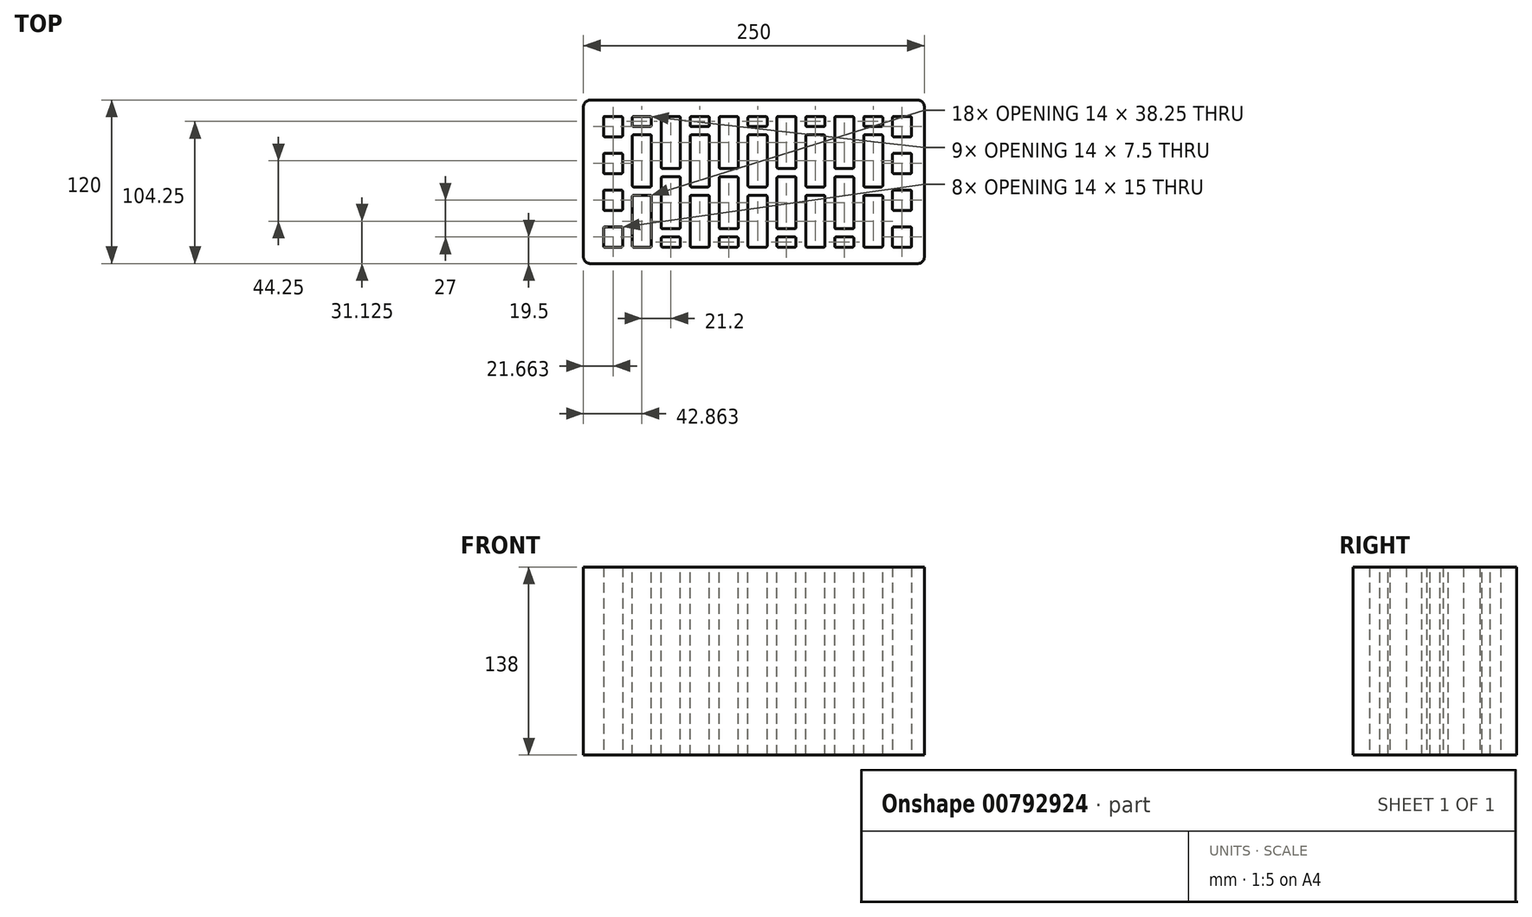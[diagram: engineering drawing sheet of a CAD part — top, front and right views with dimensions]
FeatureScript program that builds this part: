
annotation { "Feature Type Name" : "Feature", "Feature Type Description" : "" }
export const myFeature = defineFeature(function(context is Context, id is Id, definition is map)
    precondition{}
    {
        {
            var Q0;
            Q0=qCreatedBy(makeId("Top.planeOp"),FACE);
            var sketch = newSketch(context, id + "F0", { "sketchPlane" : qUnion([Q0])});
            skLineSegment(sketch, "E0.bottom", {"start": v(120, 60) * mm, "end": v(-120, 60) * mm});
            skLineSegment(sketch, "E0.top", {"start": v(120, -60) * mm, "end": v(-120, -60) * mm});
            skLineSegment(sketch, "E0.left", {"start": v(125, 55) * mm, "end": v(125, -55) * mm});
            skLineSegment(sketch, "E0.right", {"start": v(-125, 55) * mm, "end": v(-125, -55) * mm});
            skPoint(sketch, "E0.middle", {"position": v(0, 0) * mm});
            skPoint(sketch, "E1.visualSharp", {"position": v(-125, 60) * mm});
            skArc(sketch, "E1.filletArc", {"start": v(-120, 60) * mm, "mid": v(-123.54, 58.54) * mm, "end": v(-125, 55) * mm});
            skPoint(sketch, "E2.visualSharp", {"position": v(-125, -60) * mm});
            skArc(sketch, "E2.filletArc", {"start": v(-125, -55) * mm, "mid": v(-123.54, -58.54) * mm, "end": v(-120, -60) * mm});
            skPoint(sketch, "E3.visualSharp", {"position": v(125, -60) * mm});
            skArc(sketch, "E3.filletArc", {"start": v(120, -60) * mm, "mid": v(123.54, -58.54) * mm, "end": v(125, -55) * mm});
            skPoint(sketch, "E4.visualSharp", {"position": v(125, 60) * mm});
            skArc(sketch, "E4.filletArc", {"start": v(125, 55) * mm, "mid": v(123.54, 58.54) * mm, "end": v(120, 60) * mm});
            skLineSegment(sketch, "E5.bottom", {"start": v(-97.34, 48) * mm, "end": v(-109.34, 48) * mm});
            skLineSegment(sketch, "E5.top", {"start": v(-97.34, 33) * mm, "end": v(-109.34, 33) * mm});
            skLineSegment(sketch, "E5.left", {"start": v(-96.34, 47) * mm, "end": v(-96.34, 34) * mm});
            skLineSegment(sketch, "E5.right", {"start": v(-110.34, 47) * mm, "end": v(-110.34, 34) * mm});
            skPoint(sketch, "E5.middle", {"position": v(-103.34, 40.5) * mm});
            skPoint(sketch, "E6.visualSharp", {"position": v(-110.34, 48) * mm});
            skArc(sketch, "E6.filletArc", {"start": v(-109.34, 48) * mm, "mid": v(-110.04, 47.7) * mm, "end": v(-110.34, 47) * mm});
            skPoint(sketch, "E7.visualSharp", {"position": v(-96.34, 48) * mm});
            skArc(sketch, "E7.filletArc", {"start": v(-96.34, 47) * mm, "mid": v(-96.63, 47.7) * mm, "end": v(-97.34, 48) * mm});
            skPoint(sketch, "E8.visualSharp", {"position": v(-96.34, 33) * mm});
            skArc(sketch, "E8.filletArc", {"start": v(-97.34, 33) * mm, "mid": v(-96.63, 33.3) * mm, "end": v(-96.34, 34) * mm});
            skPoint(sketch, "E9.visualSharp", {"position": v(-110.34, 33) * mm});
            skArc(sketch, "E9.filletArc", {"start": v(-110.34, 34) * mm, "mid": v(-110.04, 33.3) * mm, "end": v(-109.34, 33) * mm});
            skPoint(sketch, "E10.0.1.0", {"position": v(-103.34, 13.5) * mm});
            skLineSegment(sketch, "E10.0.1.1", {"start": v(-97.34, 21) * mm, "end": v(-109.34, 21) * mm});
            skPoint(sketch, "E10.0.1.2", {"position": v(-110.34, 6) * mm});
            skLineSegment(sketch, "E10.0.1.3", {"start": v(-97.34, 6) * mm, "end": v(-109.34, 6) * mm});
            skLineSegment(sketch, "E10.0.1.4", {"start": v(-96.34, 20) * mm, "end": v(-96.34, 7) * mm});
            skLineSegment(sketch, "E10.0.1.5", {"start": v(-110.34, 20) * mm, "end": v(-110.34, 7) * mm});
            skPoint(sketch, "E10.0.1.6", {"position": v(-110.34, 21) * mm});
            skPoint(sketch, "E10.0.1.7", {"position": v(-96.34, 21) * mm});
            skPoint(sketch, "E10.0.1.8", {"position": v(-96.34, 6) * mm});
            skArc(sketch, "E10.0.1.9", {"start": v(-97.34, 6) * mm, "mid": v(-96.63, 6.3) * mm, "end": v(-96.34, 7) * mm});
            skArc(sketch, "E10.0.1.10", {"start": v(-110.34, 7) * mm, "mid": v(-110.04, 6.3) * mm, "end": v(-109.34, 6) * mm});
            skArc(sketch, "E10.0.1.11", {"start": v(-109.34, 21) * mm, "mid": v(-110.04, 20.7) * mm, "end": v(-110.34, 20) * mm});
            skArc(sketch, "E10.0.1.12", {"start": v(-96.34, 20) * mm, "mid": v(-96.63, 20.7) * mm, "end": v(-97.34, 21) * mm});
            skPoint(sketch, "E10.0.2.0", {"position": v(-103.34, -13.5) * mm});
            skLineSegment(sketch, "E10.0.2.1", {"start": v(-97.34, -6) * mm, "end": v(-109.34, -6) * mm});
            skPoint(sketch, "E10.0.2.2", {"position": v(-110.34, -21) * mm});
            skLineSegment(sketch, "E10.0.2.3", {"start": v(-97.34, -21) * mm, "end": v(-109.34, -21) * mm});
            skLineSegment(sketch, "E10.0.2.4", {"start": v(-96.34, -7) * mm, "end": v(-96.34, -20) * mm});
            skLineSegment(sketch, "E10.0.2.5", {"start": v(-110.34, -7) * mm, "end": v(-110.34, -20) * mm});
            skPoint(sketch, "E10.0.2.6", {"position": v(-110.34, -6) * mm});
            skPoint(sketch, "E10.0.2.7", {"position": v(-96.34, -6) * mm});
            skPoint(sketch, "E10.0.2.8", {"position": v(-96.34, -21) * mm});
            skArc(sketch, "E10.0.2.9", {"start": v(-97.34, -21) * mm, "mid": v(-96.63, -20.7) * mm, "end": v(-96.34, -20) * mm});
            skArc(sketch, "E10.0.2.10", {"start": v(-110.34, -20) * mm, "mid": v(-110.04, -20.7) * mm, "end": v(-109.34, -21) * mm});
            skArc(sketch, "E10.0.2.11", {"start": v(-109.34, -6) * mm, "mid": v(-110.04, -6.3) * mm, "end": v(-110.34, -7) * mm});
            skArc(sketch, "E10.0.2.12", {"start": v(-96.34, -7) * mm, "mid": v(-96.63, -6.3) * mm, "end": v(-97.34, -6) * mm});
            skPoint(sketch, "E10.0.3.0", {"position": v(-103.34, -40.5) * mm});
            skLineSegment(sketch, "E10.0.3.1", {"start": v(-97.34, -33) * mm, "end": v(-109.34, -33) * mm});
            skPoint(sketch, "E10.0.3.2", {"position": v(-110.34, -48) * mm});
            skLineSegment(sketch, "E10.0.3.3", {"start": v(-97.34, -48) * mm, "end": v(-109.34, -48) * mm});
            skLineSegment(sketch, "E10.0.3.4", {"start": v(-96.34, -34) * mm, "end": v(-96.34, -47) * mm});
            skLineSegment(sketch, "E10.0.3.5", {"start": v(-110.34, -34) * mm, "end": v(-110.34, -47) * mm});
            skPoint(sketch, "E10.0.3.6", {"position": v(-110.34, -33) * mm});
            skPoint(sketch, "E10.0.3.7", {"position": v(-96.34, -33) * mm});
            skPoint(sketch, "E10.0.3.8", {"position": v(-96.34, -48) * mm});
            skArc(sketch, "E10.0.3.9", {"start": v(-97.34, -48) * mm, "mid": v(-96.63, -47.7) * mm, "end": v(-96.34, -47) * mm});
            skArc(sketch, "E10.0.3.10", {"start": v(-110.34, -47) * mm, "mid": v(-110.04, -47.7) * mm, "end": v(-109.34, -48) * mm});
            skArc(sketch, "E10.0.3.11", {"start": v(-109.34, -33) * mm, "mid": v(-110.04, -33.3) * mm, "end": v(-110.34, -34) * mm});
            skArc(sketch, "E10.0.3.12", {"start": v(-96.34, -34) * mm, "mid": v(-96.63, -33.3) * mm, "end": v(-97.34, -33) * mm});
            skPoint(sketch, "E10.1.0.0", {"position": v(108.66, 40.5) * mm});
            skLineSegment(sketch, "E10.1.0.1", {"start": v(114.66, 48) * mm, "end": v(102.66, 48) * mm});
            skPoint(sketch, "E10.1.0.2", {"position": v(101.66, 33) * mm});
            skLineSegment(sketch, "E10.1.0.3", {"start": v(114.66, 33) * mm, "end": v(102.66, 33) * mm});
            skLineSegment(sketch, "E10.1.0.4", {"start": v(115.66, 47) * mm, "end": v(115.66, 34) * mm});
            skLineSegment(sketch, "E10.1.0.5", {"start": v(101.66, 47) * mm, "end": v(101.66, 34) * mm});
            skPoint(sketch, "E10.1.0.6", {"position": v(101.66, 48) * mm});
            skPoint(sketch, "E10.1.0.7", {"position": v(115.66, 48) * mm});
            skPoint(sketch, "E10.1.0.8", {"position": v(115.66, 33) * mm});
            skArc(sketch, "E10.1.0.9", {"start": v(114.66, 33) * mm, "mid": v(115.37, 33.3) * mm, "end": v(115.66, 34) * mm});
            skArc(sketch, "E10.1.0.10", {"start": v(101.66, 34) * mm, "mid": v(101.96, 33.3) * mm, "end": v(102.66, 33) * mm});
            skArc(sketch, "E10.1.0.11", {"start": v(102.66, 48) * mm, "mid": v(101.96, 47.7) * mm, "end": v(101.66, 47) * mm});
            skArc(sketch, "E10.1.0.12", {"start": v(115.66, 47) * mm, "mid": v(115.37, 47.7) * mm, "end": v(114.66, 48) * mm});
            skPoint(sketch, "E10.1.1.0", {"position": v(108.66, 13.5) * mm});
            skLineSegment(sketch, "E10.1.1.1", {"start": v(114.66, 21) * mm, "end": v(102.66, 21) * mm});
            skPoint(sketch, "E10.1.1.2", {"position": v(101.66, 6) * mm});
            skLineSegment(sketch, "E10.1.1.3", {"start": v(114.66, 6) * mm, "end": v(102.66, 6) * mm});
            skLineSegment(sketch, "E10.1.1.4", {"start": v(115.66, 20) * mm, "end": v(115.66, 7) * mm});
            skLineSegment(sketch, "E10.1.1.5", {"start": v(101.66, 20) * mm, "end": v(101.66, 7) * mm});
            skPoint(sketch, "E10.1.1.6", {"position": v(101.66, 21) * mm});
            skPoint(sketch, "E10.1.1.7", {"position": v(115.66, 21) * mm});
            skPoint(sketch, "E10.1.1.8", {"position": v(115.66, 6) * mm});
            skArc(sketch, "E10.1.1.9", {"start": v(114.66, 6) * mm, "mid": v(115.37, 6.3) * mm, "end": v(115.66, 7) * mm});
            skArc(sketch, "E10.1.1.10", {"start": v(101.66, 7) * mm, "mid": v(101.96, 6.3) * mm, "end": v(102.66, 6) * mm});
            skArc(sketch, "E10.1.1.11", {"start": v(102.66, 21) * mm, "mid": v(101.96, 20.7) * mm, "end": v(101.66, 20) * mm});
            skArc(sketch, "E10.1.1.12", {"start": v(115.66, 20) * mm, "mid": v(115.37, 20.7) * mm, "end": v(114.66, 21) * mm});
            skPoint(sketch, "E10.1.2.0", {"position": v(108.66, -13.5) * mm});
            skLineSegment(sketch, "E10.1.2.1", {"start": v(114.66, -6) * mm, "end": v(102.66, -6) * mm});
            skPoint(sketch, "E10.1.2.2", {"position": v(101.66, -21) * mm});
            skLineSegment(sketch, "E10.1.2.3", {"start": v(114.66, -21) * mm, "end": v(102.66, -21) * mm});
            skLineSegment(sketch, "E10.1.2.4", {"start": v(115.66, -7) * mm, "end": v(115.66, -20) * mm});
            skLineSegment(sketch, "E10.1.2.5", {"start": v(101.66, -7) * mm, "end": v(101.66, -20) * mm});
            skPoint(sketch, "E10.1.2.6", {"position": v(101.66, -6) * mm});
            skPoint(sketch, "E10.1.2.7", {"position": v(115.66, -6) * mm});
            skPoint(sketch, "E10.1.2.8", {"position": v(115.66, -21) * mm});
            skArc(sketch, "E10.1.2.9", {"start": v(114.66, -21) * mm, "mid": v(115.37, -20.7) * mm, "end": v(115.66, -20) * mm});
            skArc(sketch, "E10.1.2.10", {"start": v(101.66, -20) * mm, "mid": v(101.96, -20.7) * mm, "end": v(102.66, -21) * mm});
            skArc(sketch, "E10.1.2.11", {"start": v(102.66, -6) * mm, "mid": v(101.96, -6.3) * mm, "end": v(101.66, -7) * mm});
            skArc(sketch, "E10.1.2.12", {"start": v(115.66, -7) * mm, "mid": v(115.37, -6.3) * mm, "end": v(114.66, -6) * mm});
            skPoint(sketch, "E10.1.3.0", {"position": v(108.66, -40.5) * mm});
            skLineSegment(sketch, "E10.1.3.1", {"start": v(114.66, -33) * mm, "end": v(102.66, -33) * mm});
            skPoint(sketch, "E10.1.3.2", {"position": v(101.66, -48) * mm});
            skLineSegment(sketch, "E10.1.3.3", {"start": v(114.66, -48) * mm, "end": v(102.66, -48) * mm});
            skLineSegment(sketch, "E10.1.3.4", {"start": v(115.66, -34) * mm, "end": v(115.66, -47) * mm});
            skLineSegment(sketch, "E10.1.3.5", {"start": v(101.66, -34) * mm, "end": v(101.66, -47) * mm});
            skPoint(sketch, "E10.1.3.6", {"position": v(101.66, -33) * mm});
            skPoint(sketch, "E10.1.3.7", {"position": v(115.66, -33) * mm});
            skPoint(sketch, "E10.1.3.8", {"position": v(115.66, -48) * mm});
            skArc(sketch, "E10.1.3.9", {"start": v(114.66, -48) * mm, "mid": v(115.37, -47.7) * mm, "end": v(115.66, -47) * mm});
            skArc(sketch, "E10.1.3.10", {"start": v(101.66, -47) * mm, "mid": v(101.96, -47.7) * mm, "end": v(102.66, -48) * mm});
            skArc(sketch, "E10.1.3.11", {"start": v(102.66, -33) * mm, "mid": v(101.96, -33.3) * mm, "end": v(101.66, -34) * mm});
            skArc(sketch, "E10.1.3.12", {"start": v(115.66, -34) * mm, "mid": v(115.37, -33.3) * mm, "end": v(114.66, -33) * mm});
            skLineSegment(sketch, "E10.direction1", {"start": v(-110.34, 33) * mm, "end": v(101.66, 33) * mm, "construction": true});
            skLineSegment(sketch, "E10.direction2", {"start": v(-110.34, 33) * mm, "end": v(-110.34, 6) * mm, "construction": true});
            skLineSegment(sketch, "E11", {"start": v(-103.56, -60) * mm, "end": v(-103.56, -48) * mm, "construction": true});
            skLineSegment(sketch, "E12", {"start": v(-103.34, -33) * mm, "end": v(-103.34, -21) * mm, "construction": true});
            skLineSegment(sketch, "E13", {"start": v(-103.34, -6) * mm, "end": v(-103.34, 6) * mm, "construction": true});
            skLineSegment(sketch, "E14", {"start": v(-103.34, 21) * mm, "end": v(-103.34, 33) * mm, "construction": true});
            skLineSegment(sketch, "E15", {"start": v(-103.34, 48) * mm, "end": v(-103.34, 60) * mm, "construction": true});
            skSolve(sketch);
        }
        {
            var Q0;
            Q0=makeQuery(id+"F0.imprint","IMPRINT",FACE,{"disambiguationData":[TD([[makeQuery(id+"F0.imprint","IMPRINT",EDGE,{"derivedFrom":sQuery(id+"F0.wireOp",EDGE,"E0.bottom")}),1.0]])]});
            extrude(context, id + "F1", {"entities" : qUnion([Q0]), "depth" : 138 * mm, "offsetDistance" : 25 * mm});
        }
        {
            var Q0;
            Q0=makeQuery(id+"F1.opExtrude","CAP_FACE",FACE,{"disambiguationData":[OSD([sQuery(id+"F0.wireOp",EDGE,"E0.bottom"),sQuery(id+"F0.wireOp",EDGE,"E0.top"),sQuery(id+"F0.wireOp",EDGE,"E0.left"),sQuery(id+"F0.wireOp",EDGE,"E0.right"),sQuery(id+"F0.wireOp",EDGE,"E1.filletArc"),sQuery(id+"F0.wireOp",EDGE,"E2.filletArc"),sQuery(id+"F0.wireOp",EDGE,"E3.filletArc"),sQuery(id+"F0.wireOp",EDGE,"E4.filletArc"),sQuery(id+"F0.wireOp",EDGE,"E5.bottom"),sQuery(id+"F0.wireOp",EDGE,"E5.top"),sQuery(id+"F0.wireOp",EDGE,"E5.left"),sQuery(id+"F0.wireOp",EDGE,"E5.right"),sQuery(id+"F0.wireOp",EDGE,"E6.filletArc"),sQuery(id+"F0.wireOp",EDGE,"E7.filletArc"),sQuery(id+"F0.wireOp",EDGE,"E8.filletArc"),sQuery(id+"F0.wireOp",EDGE,"E9.filletArc"),sQuery(id+"F0.wireOp",EDGE,"E10.0.1.1"),sQuery(id+"F0.wireOp",EDGE,"E10.0.1.3"),sQuery(id+"F0.wireOp",EDGE,"E10.0.1.4"),sQuery(id+"F0.wireOp",EDGE,"E10.0.1.5"),sQuery(id+"F0.wireOp",EDGE,"E10.0.1.9"),sQuery(id+"F0.wireOp",EDGE,"E10.0.1.10"),sQuery(id+"F0.wireOp",EDGE,"E10.0.1.11"),sQuery(id+"F0.wireOp",EDGE,"E10.0.1.12"),sQuery(id+"F0.wireOp",EDGE,"E10.0.2.1"),sQuery(id+"F0.wireOp",EDGE,"E10.0.2.3"),sQuery(id+"F0.wireOp",EDGE,"E10.0.2.4"),sQuery(id+"F0.wireOp",EDGE,"E10.0.2.5"),sQuery(id+"F0.wireOp",EDGE,"E10.0.2.9"),sQuery(id+"F0.wireOp",EDGE,"E10.0.2.10"),sQuery(id+"F0.wireOp",EDGE,"E10.0.2.11"),sQuery(id+"F0.wireOp",EDGE,"E10.0.2.12"),sQuery(id+"F0.wireOp",EDGE,"E10.0.3.1"),sQuery(id+"F0.wireOp",EDGE,"E10.0.3.3"),sQuery(id+"F0.wireOp",EDGE,"E10.0.3.4"),sQuery(id+"F0.wireOp",EDGE,"E10.0.3.5"),sQuery(id+"F0.wireOp",EDGE,"E10.0.3.9"),sQuery(id+"F0.wireOp",EDGE,"E10.0.3.10"),sQuery(id+"F0.wireOp",EDGE,"E10.0.3.11"),sQuery(id+"F0.wireOp",EDGE,"E10.0.3.12"),sQuery(id+"F0.wireOp",EDGE,"E10.1.0.1"),sQuery(id+"F0.wireOp",EDGE,"E10.1.0.3"),sQuery(id+"F0.wireOp",EDGE,"E10.1.0.4"),sQuery(id+"F0.wireOp",EDGE,"E10.1.0.5"),sQuery(id+"F0.wireOp",EDGE,"E10.1.0.9"),sQuery(id+"F0.wireOp",EDGE,"E10.1.0.10"),sQuery(id+"F0.wireOp",EDGE,"E10.1.0.11"),sQuery(id+"F0.wireOp",EDGE,"E10.1.0.12"),sQuery(id+"F0.wireOp",EDGE,"E10.1.1.1"),sQuery(id+"F0.wireOp",EDGE,"E10.1.1.3"),sQuery(id+"F0.wireOp",EDGE,"E10.1.1.4"),sQuery(id+"F0.wireOp",EDGE,"E10.1.1.5"),sQuery(id+"F0.wireOp",EDGE,"E10.1.1.9"),sQuery(id+"F0.wireOp",EDGE,"E10.1.1.10"),sQuery(id+"F0.wireOp",EDGE,"E10.1.1.11"),sQuery(id+"F0.wireOp",EDGE,"E10.1.1.12"),sQuery(id+"F0.wireOp",EDGE,"E10.1.2.1"),sQuery(id+"F0.wireOp",EDGE,"E10.1.2.3"),sQuery(id+"F0.wireOp",EDGE,"E10.1.2.4"),sQuery(id+"F0.wireOp",EDGE,"E10.1.2.5"),sQuery(id+"F0.wireOp",EDGE,"E10.1.2.9"),sQuery(id+"F0.wireOp",EDGE,"E10.1.2.10"),sQuery(id+"F0.wireOp",EDGE,"E10.1.2.11"),sQuery(id+"F0.wireOp",EDGE,"E10.1.2.12"),sQuery(id+"F0.wireOp",EDGE,"E10.1.3.1"),sQuery(id+"F0.wireOp",EDGE,"E10.1.3.3"),sQuery(id+"F0.wireOp",EDGE,"E10.1.3.4"),sQuery(id+"F0.wireOp",EDGE,"E10.1.3.5"),sQuery(id+"F0.wireOp",EDGE,"E10.1.3.9"),sQuery(id+"F0.wireOp",EDGE,"E10.1.3.10"),sQuery(id+"F0.wireOp",EDGE,"E10.1.3.11"),sQuery(id+"F0.wireOp",EDGE,"E10.1.3.12")])],"isStart":false});
            var sketch = newSketch(context, id + "F2", { "sketchPlane" : qUnion([Q0])});
            skLineSegment(sketch, "E16.bottom", {"start": v(-76.14, -9.75) * mm, "end": v(-88.14, -9.75) * mm});
            skLineSegment(sketch, "E16.top", {"start": v(-76.14, -48) * mm, "end": v(-88.14, -48) * mm});
            skLineSegment(sketch, "E16.left", {"start": v(-75.14, -10.75) * mm, "end": v(-75.14, -47) * mm});
            skLineSegment(sketch, "E16.right", {"start": v(-89.14, -10.75) * mm, "end": v(-89.14, -47) * mm});
            skArc(sketch, "E17.filletArc", {"start": v(-88.14, -9.75) * mm, "mid": v(-88.84, -10.04) * mm, "end": v(-89.14, -10.75) * mm});
            skArc(sketch, "E18.filletArc", {"start": v(-75.14, -10.75) * mm, "mid": v(-75.43, -10.04) * mm, "end": v(-76.14, -9.75) * mm});
            skPoint(sketch, "E19.visualSharp", {"position": v(-75.14, -48) * mm});
            skArc(sketch, "E19.filletArc", {"start": v(-76.14, -48) * mm, "mid": v(-75.43, -47.7) * mm, "end": v(-75.14, -47) * mm});
            skPoint(sketch, "E20.visualSharp", {"position": v(-89.14, -48) * mm});
            skArc(sketch, "E20.filletArc", {"start": v(-89.14, -47) * mm, "mid": v(-88.84, -47.7) * mm, "end": v(-88.14, -48) * mm});
            skLineSegment(sketch, "E21", {"start": v(-96.34, -40.5) * mm, "end": v(-89.14, -40.5) * mm, "construction": true});
            skLineSegment(sketch, "E22.bottom", {"start": v(-76.14, 34.5) * mm, "end": v(-88.14, 34.5) * mm});
            skLineSegment(sketch, "E22.top", {"start": v(-76.14, -3.75) * mm, "end": v(-88.14, -3.75) * mm});
            skLineSegment(sketch, "E22.left", {"start": v(-75.14, 33.5) * mm, "end": v(-75.14, -2.75) * mm});
            skLineSegment(sketch, "E22.right", {"start": v(-89.14, 33.5) * mm, "end": v(-89.14, -2.75) * mm});
            skArc(sketch, "E23.filletArc", {"start": v(-88.14, 34.5) * mm, "mid": v(-88.84, 34.2) * mm, "end": v(-89.14, 33.5) * mm});
            skArc(sketch, "E24.filletArc", {"start": v(-75.14, 33.5) * mm, "mid": v(-75.43, 34.2) * mm, "end": v(-76.14, 34.5) * mm});
            skArc(sketch, "E25.filletArc", {"start": v(-76.14, -3.75) * mm, "mid": v(-75.43, -3.46) * mm, "end": v(-75.14, -2.75) * mm});
            skArc(sketch, "E26.filletArc", {"start": v(-89.14, -2.75) * mm, "mid": v(-88.84, -3.46) * mm, "end": v(-88.14, -3.75) * mm});
            skLineSegment(sketch, "E27.bottom", {"start": v(-76.14, 48) * mm, "end": v(-88.14, 48) * mm});
            skLineSegment(sketch, "E27.top", {"start": v(-76.14, 40.5) * mm, "end": v(-88.14, 40.5) * mm});
            skLineSegment(sketch, "E27.left", {"start": v(-75.14, 47) * mm, "end": v(-75.14, 41.5) * mm});
            skLineSegment(sketch, "E27.right", {"start": v(-89.14, 47) * mm, "end": v(-89.14, 41.5) * mm});
            skArc(sketch, "E28.filletArc", {"start": v(-88.14, 48) * mm, "mid": v(-88.84, 47.7) * mm, "end": v(-89.14, 47) * mm});
            skArc(sketch, "E29.filletArc", {"start": v(-75.14, 47) * mm, "mid": v(-75.43, 47.7) * mm, "end": v(-76.14, 48) * mm});
            skArc(sketch, "E30.filletArc", {"start": v(-76.14, 40.5) * mm, "mid": v(-75.43, 40.8) * mm, "end": v(-75.14, 41.5) * mm});
            skArc(sketch, "E31.filletArc", {"start": v(-89.14, 41.5) * mm, "mid": v(-88.84, 40.8) * mm, "end": v(-88.14, 40.5) * mm});
            skLineSegment(sketch, "E32", {"start": v(-82.14, -9.75) * mm, "end": v(-82.14, -3.75) * mm, "construction": true});
            skLineSegment(sketch, "E33", {"start": v(-82.14, 34.5) * mm, "end": v(-82.14, 40.5) * mm, "construction": true});
            skLineSegment(sketch, "E34", {"start": v(-96.34, 44.97) * mm, "end": v(-89.14, 44.97) * mm, "construction": true});
            skPoint(sketch, "E34.endSnap0", {"position": v(-89.14, 44.25) * mm});
            skLineSegment(sketch, "E35", {"start": v(-96.34, 40.5) * mm, "end": v(-88.14, 40.5) * mm, "construction": true});
            skLineSegment(sketch, "E36.bottom", {"start": v(-66.94, 9.75) * mm, "end": v(-54.94, 9.75) * mm});
            skLineSegment(sketch, "E36.top", {"start": v(-66.94, 48) * mm, "end": v(-54.94, 48) * mm});
            skLineSegment(sketch, "E36.left", {"start": v(-67.94, 10.75) * mm, "end": v(-67.94, 47) * mm});
            skLineSegment(sketch, "E36.right", {"start": v(-53.94, 10.75) * mm, "end": v(-53.94, 47) * mm});
            skArc(sketch, "E37.filletArc", {"start": v(-54.94, 9.75) * mm, "mid": v(-54.23, 10.04) * mm, "end": v(-53.94, 10.75) * mm});
            skArc(sketch, "E38.filletArc", {"start": v(-67.94, 10.75) * mm, "mid": v(-67.64, 10.04) * mm, "end": v(-66.94, 9.75) * mm});
            skPoint(sketch, "E39.visualSharp", {"position": v(-67.94, 48) * mm});
            skArc(sketch, "E39.filletArc", {"start": v(-66.94, 48) * mm, "mid": v(-67.64, 47.7) * mm, "end": v(-67.94, 47) * mm});
            skPoint(sketch, "E40.visualSharp", {"position": v(-53.94, 48) * mm});
            skArc(sketch, "E40.filletArc", {"start": v(-53.94, 47) * mm, "mid": v(-54.23, 47.7) * mm, "end": v(-54.94, 48) * mm});
            skLineSegment(sketch, "E41.bottom", {"start": v(-66.94, -34.5) * mm, "end": v(-54.94, -34.5) * mm});
            skLineSegment(sketch, "E41.top", {"start": v(-66.94, 3.75) * mm, "end": v(-54.94, 3.75) * mm});
            skLineSegment(sketch, "E41.left", {"start": v(-67.94, -33.5) * mm, "end": v(-67.94, 2.75) * mm});
            skLineSegment(sketch, "E41.right", {"start": v(-53.94, -33.5) * mm, "end": v(-53.94, 2.75) * mm});
            skArc(sketch, "E42.filletArc", {"start": v(-54.94, -34.5) * mm, "mid": v(-54.23, -34.2) * mm, "end": v(-53.94, -33.5) * mm});
            skArc(sketch, "E43.filletArc", {"start": v(-67.94, -33.5) * mm, "mid": v(-67.64, -34.2) * mm, "end": v(-66.94, -34.5) * mm});
            skArc(sketch, "E44.filletArc", {"start": v(-66.94, 3.75) * mm, "mid": v(-67.64, 3.46) * mm, "end": v(-67.94, 2.75) * mm});
            skArc(sketch, "E45.filletArc", {"start": v(-53.94, 2.75) * mm, "mid": v(-54.23, 3.46) * mm, "end": v(-54.94, 3.75) * mm});
            skLineSegment(sketch, "E46.bottom", {"start": v(-66.94, -48) * mm, "end": v(-54.94, -48) * mm});
            skLineSegment(sketch, "E46.top", {"start": v(-66.94, -40.5) * mm, "end": v(-54.94, -40.5) * mm});
            skLineSegment(sketch, "E46.left", {"start": v(-67.94, -47) * mm, "end": v(-67.94, -41.5) * mm});
            skLineSegment(sketch, "E46.right", {"start": v(-53.94, -47) * mm, "end": v(-53.94, -41.5) * mm});
            skArc(sketch, "E47.filletArc", {"start": v(-54.94, -48) * mm, "mid": v(-54.23, -47.7) * mm, "end": v(-53.94, -47) * mm});
            skArc(sketch, "E48.filletArc", {"start": v(-67.94, -47) * mm, "mid": v(-67.64, -47.7) * mm, "end": v(-66.94, -48) * mm});
            skArc(sketch, "E49.filletArc", {"start": v(-66.94, -40.5) * mm, "mid": v(-67.64, -40.8) * mm, "end": v(-67.94, -41.5) * mm});
            skArc(sketch, "E50.filletArc", {"start": v(-53.94, -41.5) * mm, "mid": v(-54.23, -40.8) * mm, "end": v(-54.94, -40.5) * mm});
            skLineSegment(sketch, "E51", {"start": v(-60.94, 9.75) * mm, "end": v(-60.94, 3.75) * mm, "construction": true});
            skLineSegment(sketch, "E52", {"start": v(-60.94, -34.5) * mm, "end": v(-60.94, -40.5) * mm, "construction": true});
            skPoint(sketch, "E53.endSnap0", {"position": v(-53.94, -44.25) * mm});
            skLineSegment(sketch, "E54", {"start": v(-75.14, 44.25) * mm, "end": v(-67.94, 44.25) * mm, "construction": true});
            skLineSegment(sketch, "E55.1.0.0", {"start": v(-39.74, 34.5) * mm, "end": v(-39.74, 40.5) * mm, "construction": true});
            skPoint(sketch, "E55.1.0.1", {"position": v(-11.54, 48) * mm});
            skLineSegment(sketch, "E55.1.0.2", {"start": v(-33.74, 40.5) * mm, "end": v(-45.74, 40.5) * mm});
            skLineSegment(sketch, "E55.1.0.3", {"start": v(-33.74, 48) * mm, "end": v(-45.74, 48) * mm});
            skPoint(sketch, "E55.1.0.4", {"position": v(-46.74, 44.25) * mm});
            skPoint(sketch, "E55.1.0.5", {"position": v(-11.54, -44.25) * mm});
            skLineSegment(sketch, "E55.1.0.6", {"start": v(-25.54, 10.75) * mm, "end": v(-25.54, 47) * mm});
            skLineSegment(sketch, "E55.1.0.7", {"start": v(-33.74, -3.75) * mm, "end": v(-45.74, -3.75) * mm});
            skLineSegment(sketch, "E55.1.0.8", {"start": v(-24.54, 9.75) * mm, "end": v(-12.54, 9.75) * mm});
            skLineSegment(sketch, "E55.1.0.9", {"start": v(-33.74, -9.75) * mm, "end": v(-45.74, -9.75) * mm});
            skLineSegment(sketch, "E55.1.0.10", {"start": v(-24.54, -34.5) * mm, "end": v(-12.54, -34.5) * mm});
            skLineSegment(sketch, "E55.1.0.11", {"start": v(-24.54, 48) * mm, "end": v(-12.54, 48) * mm});
            skLineSegment(sketch, "E55.1.0.12", {"start": v(-46.74, -10.75) * mm, "end": v(-46.74, -47) * mm});
            skLineSegment(sketch, "E55.1.0.13", {"start": v(-24.54, -48) * mm, "end": v(-12.54, -48) * mm});
            skLineSegment(sketch, "E55.1.0.14", {"start": v(-32.74, 33.5) * mm, "end": v(-32.74, -2.75) * mm});
            skPoint(sketch, "E55.1.0.15", {"position": v(-46.74, -48) * mm});
            skPoint(sketch, "E55.1.0.16", {"position": v(-25.54, 48) * mm});
            skLineSegment(sketch, "E55.1.0.17", {"start": v(-24.54, -40.5) * mm, "end": v(-12.54, -40.5) * mm});
            skLineSegment(sketch, "E55.1.0.18", {"start": v(-11.54, 10.75) * mm, "end": v(-11.54, 47) * mm});
            skLineSegment(sketch, "E55.1.0.19", {"start": v(-32.74, 44.25) * mm, "end": v(-25.54, 44.25) * mm, "construction": true});
            skLineSegment(sketch, "E55.1.0.20", {"start": v(-11.54, -33.5) * mm, "end": v(-11.54, 2.75) * mm});
            skLineSegment(sketch, "E55.1.0.21", {"start": v(-18.54, 9.75) * mm, "end": v(-18.54, 3.75) * mm, "construction": true});
            skPoint(sketch, "E55.1.0.22", {"position": v(-32.74, -48) * mm});
            skLineSegment(sketch, "E55.1.0.23", {"start": v(-32.74, -10.75) * mm, "end": v(-32.74, -47) * mm});
            skLineSegment(sketch, "E55.1.0.24", {"start": v(-46.74, 33.5) * mm, "end": v(-46.74, -2.75) * mm});
            skLineSegment(sketch, "E55.1.0.25", {"start": v(-25.54, -47) * mm, "end": v(-25.54, -41.5) * mm});
            skLineSegment(sketch, "E55.1.0.26", {"start": v(-33.74, 34.5) * mm, "end": v(-45.74, 34.5) * mm});
            skLineSegment(sketch, "E55.1.0.27", {"start": v(-25.54, -33.5) * mm, "end": v(-25.54, 2.75) * mm});
            skLineSegment(sketch, "E55.1.0.28", {"start": v(-39.74, -9.75) * mm, "end": v(-39.74, -3.75) * mm, "construction": true});
            skLineSegment(sketch, "E55.1.0.29", {"start": v(-24.54, 3.75) * mm, "end": v(-12.54, 3.75) * mm});
            skLineSegment(sketch, "E55.1.0.30", {"start": v(-18.54, -34.5) * mm, "end": v(-18.54, -40.5) * mm, "construction": true});
            skLineSegment(sketch, "E55.1.0.31", {"start": v(-33.74, -48) * mm, "end": v(-45.74, -48) * mm});
            skLineSegment(sketch, "E55.1.0.32", {"start": v(-32.74, 47) * mm, "end": v(-32.74, 41.5) * mm});
            skLineSegment(sketch, "E55.1.0.33", {"start": v(-53.94, -40.5) * mm, "end": v(-46.74, -40.5) * mm, "construction": true});
            skLineSegment(sketch, "E55.1.0.34", {"start": v(-11.54, -47) * mm, "end": v(-11.54, -41.5) * mm});
            skArc(sketch, "E55.1.0.35", {"start": v(-45.74, 34.5) * mm, "mid": v(-46.44, 34.2) * mm, "end": v(-46.74, 33.5) * mm});
            skArc(sketch, "E55.1.0.36", {"start": v(-11.54, 2.75) * mm, "mid": v(-11.83, 3.46) * mm, "end": v(-12.54, 3.75) * mm});
            skArc(sketch, "E55.1.0.37", {"start": v(-25.54, -47) * mm, "mid": v(-25.24, -47.7) * mm, "end": v(-24.54, -48) * mm});
            skArc(sketch, "E55.1.0.38", {"start": v(-24.54, -40.5) * mm, "mid": v(-25.24, -40.8) * mm, "end": v(-25.54, -41.5) * mm});
            skArc(sketch, "E55.1.0.39", {"start": v(-12.54, 9.75) * mm, "mid": v(-11.83, 10.04) * mm, "end": v(-11.54, 10.75) * mm});
            skArc(sketch, "E55.1.0.40", {"start": v(-32.74, -10.75) * mm, "mid": v(-33.03, -10.04) * mm, "end": v(-33.74, -9.75) * mm});
            skArc(sketch, "E55.1.0.41", {"start": v(-25.54, -33.5) * mm, "mid": v(-25.24, -34.2) * mm, "end": v(-24.54, -34.5) * mm});
            skLineSegment(sketch, "E55.1.0.42", {"start": v(-53.94, 44.97) * mm, "end": v(-46.74, 44.97) * mm, "construction": true});
            skArc(sketch, "E55.1.0.43", {"start": v(-33.74, -3.75) * mm, "mid": v(-33.03, -3.46) * mm, "end": v(-32.74, -2.75) * mm});
            skArc(sketch, "E55.1.0.44", {"start": v(-24.54, 3.75) * mm, "mid": v(-25.24, 3.46) * mm, "end": v(-25.54, 2.75) * mm});
            skArc(sketch, "E55.1.0.45", {"start": v(-11.54, -41.5) * mm, "mid": v(-11.83, -40.8) * mm, "end": v(-12.54, -40.5) * mm});
            skLineSegment(sketch, "E55.1.0.46", {"start": v(-46.74, 47) * mm, "end": v(-46.74, 41.5) * mm});
            skLineSegment(sketch, "E55.1.0.47", {"start": v(-53.94, 40.5) * mm, "end": v(-45.74, 40.5) * mm, "construction": true});
            skArc(sketch, "E55.1.0.48", {"start": v(-12.54, -34.5) * mm, "mid": v(-11.83, -34.2) * mm, "end": v(-11.54, -33.5) * mm});
            skArc(sketch, "E55.1.0.49", {"start": v(-32.74, 33.5) * mm, "mid": v(-33.03, 34.2) * mm, "end": v(-33.74, 34.5) * mm});
            skArc(sketch, "E55.1.0.50", {"start": v(-12.54, -48) * mm, "mid": v(-11.83, -47.7) * mm, "end": v(-11.54, -47) * mm});
            skArc(sketch, "E55.1.0.51", {"start": v(-46.74, -2.75) * mm, "mid": v(-46.44, -3.46) * mm, "end": v(-45.74, -3.75) * mm});
            skArc(sketch, "E55.1.0.52", {"start": v(-45.74, 48) * mm, "mid": v(-46.44, 47.7) * mm, "end": v(-46.74, 47) * mm});
            skArc(sketch, "E55.1.0.53", {"start": v(-32.74, 47) * mm, "mid": v(-33.03, 47.7) * mm, "end": v(-33.74, 48) * mm});
            skArc(sketch, "E55.1.0.54", {"start": v(-45.74, -9.75) * mm, "mid": v(-46.44, -10.04) * mm, "end": v(-46.74, -10.75) * mm});
            skArc(sketch, "E55.1.0.55", {"start": v(-33.74, 40.5) * mm, "mid": v(-33.03, 40.8) * mm, "end": v(-32.74, 41.5) * mm});
            skArc(sketch, "E55.1.0.56", {"start": v(-25.54, 10.75) * mm, "mid": v(-25.24, 10.04) * mm, "end": v(-24.54, 9.75) * mm});
            skArc(sketch, "E55.1.0.57", {"start": v(-24.54, 48) * mm, "mid": v(-25.24, 47.7) * mm, "end": v(-25.54, 47) * mm});
            skArc(sketch, "E55.1.0.58", {"start": v(-11.54, 47) * mm, "mid": v(-11.83, 47.7) * mm, "end": v(-12.54, 48) * mm});
            skArc(sketch, "E55.1.0.59", {"start": v(-46.74, -47) * mm, "mid": v(-46.44, -47.7) * mm, "end": v(-45.74, -48) * mm});
            skArc(sketch, "E55.1.0.60", {"start": v(-46.74, 41.5) * mm, "mid": v(-46.44, 40.8) * mm, "end": v(-45.74, 40.5) * mm});
            skArc(sketch, "E55.1.0.61", {"start": v(-33.74, -48) * mm, "mid": v(-33.03, -47.7) * mm, "end": v(-32.74, -47) * mm});
            skLineSegment(sketch, "E55.2.0.0", {"start": v(2.66, 34.5) * mm, "end": v(2.66, 40.5) * mm, "construction": true});
            skPoint(sketch, "E55.2.0.1", {"position": v(30.86, 48) * mm});
            skLineSegment(sketch, "E55.2.0.2", {"start": v(8.66, 40.5) * mm, "end": v(-3.34, 40.5) * mm});
            skLineSegment(sketch, "E55.2.0.3", {"start": v(8.66, 48) * mm, "end": v(-3.34, 48) * mm});
            skPoint(sketch, "E55.2.0.4", {"position": v(-4.34, 44.25) * mm});
            skPoint(sketch, "E55.2.0.5", {"position": v(30.86, -44.25) * mm});
            skLineSegment(sketch, "E55.2.0.6", {"start": v(16.86, 10.75) * mm, "end": v(16.86, 47) * mm});
            skLineSegment(sketch, "E55.2.0.7", {"start": v(8.66, -3.75) * mm, "end": v(-3.34, -3.75) * mm});
            skLineSegment(sketch, "E55.2.0.8", {"start": v(17.86, 9.75) * mm, "end": v(29.86, 9.75) * mm});
            skLineSegment(sketch, "E55.2.0.9", {"start": v(8.66, -9.75) * mm, "end": v(-3.34, -9.75) * mm});
            skLineSegment(sketch, "E55.2.0.10", {"start": v(17.86, -34.5) * mm, "end": v(29.86, -34.5) * mm});
            skLineSegment(sketch, "E55.2.0.11", {"start": v(17.86, 48) * mm, "end": v(29.86, 48) * mm});
            skLineSegment(sketch, "E55.2.0.12", {"start": v(-4.34, -10.75) * mm, "end": v(-4.34, -47) * mm});
            skLineSegment(sketch, "E55.2.0.13", {"start": v(17.86, -48) * mm, "end": v(29.86, -48) * mm});
            skLineSegment(sketch, "E55.2.0.14", {"start": v(9.66, 33.5) * mm, "end": v(9.66, -2.75) * mm});
            skPoint(sketch, "E55.2.0.15", {"position": v(-4.34, -48) * mm});
            skPoint(sketch, "E55.2.0.16", {"position": v(16.86, 48) * mm});
            skLineSegment(sketch, "E55.2.0.17", {"start": v(17.86, -40.5) * mm, "end": v(29.86, -40.5) * mm});
            skLineSegment(sketch, "E55.2.0.18", {"start": v(30.86, 10.75) * mm, "end": v(30.86, 47) * mm});
            skLineSegment(sketch, "E55.2.0.19", {"start": v(9.66, 44.25) * mm, "end": v(16.86, 44.25) * mm, "construction": true});
            skLineSegment(sketch, "E55.2.0.20", {"start": v(30.86, -33.5) * mm, "end": v(30.86, 2.75) * mm});
            skLineSegment(sketch, "E55.2.0.21", {"start": v(23.86, 9.75) * mm, "end": v(23.86, 3.75) * mm, "construction": true});
            skPoint(sketch, "E55.2.0.22", {"position": v(9.66, -48) * mm});
            skLineSegment(sketch, "E55.2.0.23", {"start": v(9.66, -10.75) * mm, "end": v(9.66, -47) * mm});
            skLineSegment(sketch, "E55.2.0.24", {"start": v(-4.34, 33.5) * mm, "end": v(-4.34, -2.75) * mm});
            skLineSegment(sketch, "E55.2.0.25", {"start": v(16.86, -47) * mm, "end": v(16.86, -41.5) * mm});
            skLineSegment(sketch, "E55.2.0.26", {"start": v(8.66, 34.5) * mm, "end": v(-3.34, 34.5) * mm});
            skLineSegment(sketch, "E55.2.0.27", {"start": v(16.86, -33.5) * mm, "end": v(16.86, 2.75) * mm});
            skLineSegment(sketch, "E55.2.0.28", {"start": v(2.66, -9.75) * mm, "end": v(2.66, -3.75) * mm, "construction": true});
            skLineSegment(sketch, "E55.2.0.29", {"start": v(17.86, 3.75) * mm, "end": v(29.86, 3.75) * mm});
            skLineSegment(sketch, "E55.2.0.30", {"start": v(23.86, -34.5) * mm, "end": v(23.86, -40.5) * mm, "construction": true});
            skLineSegment(sketch, "E55.2.0.31", {"start": v(8.66, -48) * mm, "end": v(-3.34, -48) * mm});
            skLineSegment(sketch, "E55.2.0.32", {"start": v(9.66, 47) * mm, "end": v(9.66, 41.5) * mm});
            skLineSegment(sketch, "E55.2.0.33", {"start": v(-11.54, -40.5) * mm, "end": v(-4.34, -40.5) * mm, "construction": true});
            skLineSegment(sketch, "E55.2.0.34", {"start": v(30.86, -47) * mm, "end": v(30.86, -41.5) * mm});
            skArc(sketch, "E55.2.0.35", {"start": v(-3.34, 34.5) * mm, "mid": v(-4.04, 34.2) * mm, "end": v(-4.34, 33.5) * mm});
            skArc(sketch, "E55.2.0.36", {"start": v(30.86, 2.75) * mm, "mid": v(30.57, 3.46) * mm, "end": v(29.86, 3.75) * mm});
            skArc(sketch, "E55.2.0.37", {"start": v(16.86, -47) * mm, "mid": v(17.16, -47.7) * mm, "end": v(17.86, -48) * mm});
            skArc(sketch, "E55.2.0.38", {"start": v(17.86, -40.5) * mm, "mid": v(17.16, -40.8) * mm, "end": v(16.86, -41.5) * mm});
            skArc(sketch, "E55.2.0.39", {"start": v(29.86, 9.75) * mm, "mid": v(30.57, 10.04) * mm, "end": v(30.86, 10.75) * mm});
            skArc(sketch, "E55.2.0.40", {"start": v(9.66, -10.75) * mm, "mid": v(9.37, -10.04) * mm, "end": v(8.66, -9.75) * mm});
            skArc(sketch, "E55.2.0.41", {"start": v(16.86, -33.5) * mm, "mid": v(17.16, -34.2) * mm, "end": v(17.86, -34.5) * mm});
            skLineSegment(sketch, "E55.2.0.42", {"start": v(-11.54, 44.97) * mm, "end": v(-4.34, 44.97) * mm, "construction": true});
            skArc(sketch, "E55.2.0.43", {"start": v(8.66, -3.75) * mm, "mid": v(9.37, -3.46) * mm, "end": v(9.66, -2.75) * mm});
            skArc(sketch, "E55.2.0.44", {"start": v(17.86, 3.75) * mm, "mid": v(17.16, 3.46) * mm, "end": v(16.86, 2.75) * mm});
            skArc(sketch, "E55.2.0.45", {"start": v(30.86, -41.5) * mm, "mid": v(30.57, -40.8) * mm, "end": v(29.86, -40.5) * mm});
            skLineSegment(sketch, "E55.2.0.46", {"start": v(-4.34, 47) * mm, "end": v(-4.34, 41.5) * mm});
            skLineSegment(sketch, "E55.2.0.47", {"start": v(-11.54, 40.5) * mm, "end": v(-3.34, 40.5) * mm, "construction": true});
            skArc(sketch, "E55.2.0.48", {"start": v(29.86, -34.5) * mm, "mid": v(30.57, -34.2) * mm, "end": v(30.86, -33.5) * mm});
            skArc(sketch, "E55.2.0.49", {"start": v(9.66, 33.5) * mm, "mid": v(9.37, 34.2) * mm, "end": v(8.66, 34.5) * mm});
            skArc(sketch, "E55.2.0.50", {"start": v(29.86, -48) * mm, "mid": v(30.57, -47.7) * mm, "end": v(30.86, -47) * mm});
            skArc(sketch, "E55.2.0.51", {"start": v(-4.34, -2.75) * mm, "mid": v(-4.04, -3.46) * mm, "end": v(-3.34, -3.75) * mm});
            skArc(sketch, "E55.2.0.52", {"start": v(-3.34, 48) * mm, "mid": v(-4.04, 47.7) * mm, "end": v(-4.34, 47) * mm});
            skArc(sketch, "E55.2.0.53", {"start": v(9.66, 47) * mm, "mid": v(9.37, 47.7) * mm, "end": v(8.66, 48) * mm});
            skArc(sketch, "E55.2.0.54", {"start": v(-3.34, -9.75) * mm, "mid": v(-4.04, -10.04) * mm, "end": v(-4.34, -10.75) * mm});
            skArc(sketch, "E55.2.0.55", {"start": v(8.66, 40.5) * mm, "mid": v(9.37, 40.8) * mm, "end": v(9.66, 41.5) * mm});
            skArc(sketch, "E55.2.0.56", {"start": v(16.86, 10.75) * mm, "mid": v(17.16, 10.04) * mm, "end": v(17.86, 9.75) * mm});
            skArc(sketch, "E55.2.0.57", {"start": v(17.86, 48) * mm, "mid": v(17.16, 47.7) * mm, "end": v(16.86, 47) * mm});
            skArc(sketch, "E55.2.0.58", {"start": v(30.86, 47) * mm, "mid": v(30.57, 47.7) * mm, "end": v(29.86, 48) * mm});
            skArc(sketch, "E55.2.0.59", {"start": v(-4.34, -47) * mm, "mid": v(-4.04, -47.7) * mm, "end": v(-3.34, -48) * mm});
            skArc(sketch, "E55.2.0.60", {"start": v(-4.34, 41.5) * mm, "mid": v(-4.04, 40.8) * mm, "end": v(-3.34, 40.5) * mm});
            skArc(sketch, "E55.2.0.61", {"start": v(8.66, -48) * mm, "mid": v(9.37, -47.7) * mm, "end": v(9.66, -47) * mm});
            skLineSegment(sketch, "E55.3.0.0", {"start": v(45.06, 34.5) * mm, "end": v(45.06, 40.5) * mm, "construction": true});
            skPoint(sketch, "E55.3.0.1", {"position": v(73.26, 48) * mm});
            skLineSegment(sketch, "E55.3.0.2", {"start": v(51.06, 40.5) * mm, "end": v(39.06, 40.5) * mm});
            skLineSegment(sketch, "E55.3.0.3", {"start": v(51.06, 48) * mm, "end": v(39.06, 48) * mm});
            skPoint(sketch, "E55.3.0.4", {"position": v(38.06, 44.25) * mm});
            skPoint(sketch, "E55.3.0.5", {"position": v(73.26, -44.25) * mm});
            skLineSegment(sketch, "E55.3.0.6", {"start": v(59.26, 10.75) * mm, "end": v(59.26, 47) * mm});
            skLineSegment(sketch, "E55.3.0.7", {"start": v(51.06, -3.75) * mm, "end": v(39.06, -3.75) * mm});
            skLineSegment(sketch, "E55.3.0.8", {"start": v(60.26, 9.75) * mm, "end": v(72.26, 9.75) * mm});
            skLineSegment(sketch, "E55.3.0.9", {"start": v(51.06, -9.75) * mm, "end": v(39.06, -9.75) * mm});
            skLineSegment(sketch, "E55.3.0.10", {"start": v(60.26, -34.5) * mm, "end": v(72.26, -34.5) * mm});
            skLineSegment(sketch, "E55.3.0.11", {"start": v(60.26, 48) * mm, "end": v(72.26, 48) * mm});
            skLineSegment(sketch, "E55.3.0.12", {"start": v(38.06, -10.75) * mm, "end": v(38.06, -47) * mm});
            skLineSegment(sketch, "E55.3.0.13", {"start": v(60.26, -48) * mm, "end": v(72.26, -48) * mm});
            skLineSegment(sketch, "E55.3.0.14", {"start": v(52.06, 33.5) * mm, "end": v(52.06, -2.75) * mm});
            skPoint(sketch, "E55.3.0.15", {"position": v(38.06, -48) * mm});
            skPoint(sketch, "E55.3.0.16", {"position": v(59.26, 48) * mm});
            skLineSegment(sketch, "E55.3.0.17", {"start": v(60.26, -40.5) * mm, "end": v(72.26, -40.5) * mm});
            skLineSegment(sketch, "E55.3.0.18", {"start": v(73.26, 10.75) * mm, "end": v(73.26, 47) * mm});
            skLineSegment(sketch, "E55.3.0.19", {"start": v(52.06, 44.25) * mm, "end": v(59.26, 44.25) * mm, "construction": true});
            skLineSegment(sketch, "E55.3.0.20", {"start": v(73.26, -33.5) * mm, "end": v(73.26, 2.75) * mm});
            skLineSegment(sketch, "E55.3.0.21", {"start": v(66.26, 9.75) * mm, "end": v(66.26, 3.75) * mm, "construction": true});
            skPoint(sketch, "E55.3.0.22", {"position": v(52.06, -48) * mm});
            skLineSegment(sketch, "E55.3.0.23", {"start": v(52.06, -10.75) * mm, "end": v(52.06, -47) * mm});
            skLineSegment(sketch, "E55.3.0.24", {"start": v(38.06, 33.5) * mm, "end": v(38.06, -2.75) * mm});
            skLineSegment(sketch, "E55.3.0.25", {"start": v(59.26, -47) * mm, "end": v(59.26, -41.5) * mm});
            skLineSegment(sketch, "E55.3.0.26", {"start": v(51.06, 34.5) * mm, "end": v(39.06, 34.5) * mm});
            skLineSegment(sketch, "E55.3.0.27", {"start": v(59.26, -33.5) * mm, "end": v(59.26, 2.75) * mm});
            skLineSegment(sketch, "E55.3.0.28", {"start": v(45.06, -9.75) * mm, "end": v(45.06, -3.75) * mm, "construction": true});
            skLineSegment(sketch, "E55.3.0.29", {"start": v(60.26, 3.75) * mm, "end": v(72.26, 3.75) * mm});
            skLineSegment(sketch, "E55.3.0.30", {"start": v(66.26, -34.5) * mm, "end": v(66.26, -40.5) * mm, "construction": true});
            skLineSegment(sketch, "E55.3.0.31", {"start": v(51.06, -48) * mm, "end": v(39.06, -48) * mm});
            skLineSegment(sketch, "E55.3.0.32", {"start": v(52.06, 47) * mm, "end": v(52.06, 41.5) * mm});
            skLineSegment(sketch, "E55.3.0.33", {"start": v(30.86, -40.5) * mm, "end": v(38.06, -40.5) * mm, "construction": true});
            skLineSegment(sketch, "E55.3.0.34", {"start": v(73.26, -47) * mm, "end": v(73.26, -41.5) * mm});
            skArc(sketch, "E55.3.0.35", {"start": v(39.06, 34.5) * mm, "mid": v(38.36, 34.2) * mm, "end": v(38.06, 33.5) * mm});
            skArc(sketch, "E55.3.0.36", {"start": v(73.26, 2.75) * mm, "mid": v(72.97, 3.46) * mm, "end": v(72.26, 3.75) * mm});
            skArc(sketch, "E55.3.0.37", {"start": v(59.26, -47) * mm, "mid": v(59.56, -47.7) * mm, "end": v(60.26, -48) * mm});
            skArc(sketch, "E55.3.0.38", {"start": v(60.26, -40.5) * mm, "mid": v(59.56, -40.8) * mm, "end": v(59.26, -41.5) * mm});
            skArc(sketch, "E55.3.0.39", {"start": v(72.26, 9.75) * mm, "mid": v(72.97, 10.04) * mm, "end": v(73.26, 10.75) * mm});
            skArc(sketch, "E55.3.0.40", {"start": v(52.06, -10.75) * mm, "mid": v(51.77, -10.04) * mm, "end": v(51.06, -9.75) * mm});
            skArc(sketch, "E55.3.0.41", {"start": v(59.26, -33.5) * mm, "mid": v(59.56, -34.2) * mm, "end": v(60.26, -34.5) * mm});
            skLineSegment(sketch, "E55.3.0.42", {"start": v(30.86, 44.97) * mm, "end": v(38.06, 44.97) * mm, "construction": true});
            skArc(sketch, "E55.3.0.43", {"start": v(51.06, -3.75) * mm, "mid": v(51.77, -3.46) * mm, "end": v(52.06, -2.75) * mm});
            skArc(sketch, "E55.3.0.44", {"start": v(60.26, 3.75) * mm, "mid": v(59.56, 3.46) * mm, "end": v(59.26, 2.75) * mm});
            skArc(sketch, "E55.3.0.45", {"start": v(73.26, -41.5) * mm, "mid": v(72.97, -40.8) * mm, "end": v(72.26, -40.5) * mm});
            skLineSegment(sketch, "E55.3.0.46", {"start": v(38.06, 47) * mm, "end": v(38.06, 41.5) * mm});
            skLineSegment(sketch, "E55.3.0.47", {"start": v(30.86, 40.5) * mm, "end": v(39.06, 40.5) * mm, "construction": true});
            skArc(sketch, "E55.3.0.48", {"start": v(72.26, -34.5) * mm, "mid": v(72.97, -34.2) * mm, "end": v(73.26, -33.5) * mm});
            skArc(sketch, "E55.3.0.49", {"start": v(52.06, 33.5) * mm, "mid": v(51.77, 34.2) * mm, "end": v(51.06, 34.5) * mm});
            skArc(sketch, "E55.3.0.50", {"start": v(72.26, -48) * mm, "mid": v(72.97, -47.7) * mm, "end": v(73.26, -47) * mm});
            skArc(sketch, "E55.3.0.51", {"start": v(38.06, -2.75) * mm, "mid": v(38.36, -3.46) * mm, "end": v(39.06, -3.75) * mm});
            skArc(sketch, "E55.3.0.52", {"start": v(39.06, 48) * mm, "mid": v(38.36, 47.7) * mm, "end": v(38.06, 47) * mm});
            skArc(sketch, "E55.3.0.53", {"start": v(52.06, 47) * mm, "mid": v(51.77, 47.7) * mm, "end": v(51.06, 48) * mm});
            skArc(sketch, "E55.3.0.54", {"start": v(39.06, -9.75) * mm, "mid": v(38.36, -10.04) * mm, "end": v(38.06, -10.75) * mm});
            skArc(sketch, "E55.3.0.55", {"start": v(51.06, 40.5) * mm, "mid": v(51.77, 40.8) * mm, "end": v(52.06, 41.5) * mm});
            skArc(sketch, "E55.3.0.56", {"start": v(59.26, 10.75) * mm, "mid": v(59.56, 10.04) * mm, "end": v(60.26, 9.75) * mm});
            skArc(sketch, "E55.3.0.57", {"start": v(60.26, 48) * mm, "mid": v(59.56, 47.7) * mm, "end": v(59.26, 47) * mm});
            skArc(sketch, "E55.3.0.58", {"start": v(73.26, 47) * mm, "mid": v(72.97, 47.7) * mm, "end": v(72.26, 48) * mm});
            skArc(sketch, "E55.3.0.59", {"start": v(38.06, -47) * mm, "mid": v(38.36, -47.7) * mm, "end": v(39.06, -48) * mm});
            skArc(sketch, "E55.3.0.60", {"start": v(38.06, 41.5) * mm, "mid": v(38.36, 40.8) * mm, "end": v(39.06, 40.5) * mm});
            skArc(sketch, "E55.3.0.61", {"start": v(51.06, -48) * mm, "mid": v(51.77, -47.7) * mm, "end": v(52.06, -47) * mm});
            skLineSegment(sketch, "E55.4.0.0", {"start": v(87.46, 34.5) * mm, "end": v(87.46, 40.5) * mm, "construction": true});
            skLineSegment(sketch, "E55.4.0.2", {"start": v(93.46, 40.5) * mm, "end": v(81.46, 40.5) * mm});
            skLineSegment(sketch, "E55.4.0.3", {"start": v(93.46, 48) * mm, "end": v(81.46, 48) * mm});
            skPoint(sketch, "E55.4.0.4", {"position": v(80.46, 44.25) * mm});
            skLineSegment(sketch, "E55.4.0.7", {"start": v(93.46, -3.75) * mm, "end": v(81.46, -3.75) * mm});
            skLineSegment(sketch, "E55.4.0.9", {"start": v(93.46, -9.75) * mm, "end": v(81.46, -9.75) * mm});
            skLineSegment(sketch, "E55.4.0.12", {"start": v(80.46, -10.75) * mm, "end": v(80.46, -47) * mm});
            skLineSegment(sketch, "E55.4.0.14", {"start": v(94.46, 33.5) * mm, "end": v(94.46, -2.75) * mm});
            skPoint(sketch, "E55.4.0.15", {"position": v(80.46, -48) * mm});
            skLineSegment(sketch, "E55.4.0.19", {"start": v(94.46, 44.25) * mm, "end": v(101.66, 44.25) * mm, "construction": true});
            skPoint(sketch, "E55.4.0.22", {"position": v(94.46, -48) * mm});
            skLineSegment(sketch, "E55.4.0.23", {"start": v(94.46, -10.75) * mm, "end": v(94.46, -47) * mm});
            skLineSegment(sketch, "E55.4.0.24", {"start": v(80.46, 33.5) * mm, "end": v(80.46, -2.75) * mm});
            skLineSegment(sketch, "E55.4.0.26", {"start": v(93.46, 34.5) * mm, "end": v(81.46, 34.5) * mm});
            skLineSegment(sketch, "E55.4.0.28", {"start": v(87.46, -9.75) * mm, "end": v(87.46, -3.75) * mm, "construction": true});
            skLineSegment(sketch, "E55.4.0.31", {"start": v(93.46, -48) * mm, "end": v(81.46, -48) * mm});
            skLineSegment(sketch, "E55.4.0.32", {"start": v(94.46, 47) * mm, "end": v(94.46, 41.5) * mm});
            skLineSegment(sketch, "E55.4.0.33", {"start": v(73.26, -40.5) * mm, "end": v(80.46, -40.5) * mm, "construction": true});
            skArc(sketch, "E55.4.0.35", {"start": v(81.46, 34.5) * mm, "mid": v(80.76, 34.2) * mm, "end": v(80.46, 33.5) * mm});
            skArc(sketch, "E55.4.0.40", {"start": v(94.46, -10.75) * mm, "mid": v(94.17, -10.04) * mm, "end": v(93.46, -9.75) * mm});
            skLineSegment(sketch, "E55.4.0.42", {"start": v(73.26, 44.97) * mm, "end": v(80.46, 44.97) * mm, "construction": true});
            skArc(sketch, "E55.4.0.43", {"start": v(93.46, -3.75) * mm, "mid": v(94.17, -3.46) * mm, "end": v(94.46, -2.75) * mm});
            skLineSegment(sketch, "E55.4.0.46", {"start": v(80.46, 47) * mm, "end": v(80.46, 41.5) * mm});
            skLineSegment(sketch, "E55.4.0.47", {"start": v(73.26, 40.5) * mm, "end": v(81.46, 40.5) * mm, "construction": true});
            skArc(sketch, "E55.4.0.49", {"start": v(94.46, 33.5) * mm, "mid": v(94.17, 34.2) * mm, "end": v(93.46, 34.5) * mm});
            skArc(sketch, "E55.4.0.51", {"start": v(80.46, -2.75) * mm, "mid": v(80.76, -3.46) * mm, "end": v(81.46, -3.75) * mm});
            skArc(sketch, "E55.4.0.52", {"start": v(81.46, 48) * mm, "mid": v(80.76, 47.7) * mm, "end": v(80.46, 47) * mm});
            skArc(sketch, "E55.4.0.53", {"start": v(94.46, 47) * mm, "mid": v(94.17, 47.7) * mm, "end": v(93.46, 48) * mm});
            skArc(sketch, "E55.4.0.54", {"start": v(81.46, -9.75) * mm, "mid": v(80.76, -10.04) * mm, "end": v(80.46, -10.75) * mm});
            skArc(sketch, "E55.4.0.55", {"start": v(93.46, 40.5) * mm, "mid": v(94.17, 40.8) * mm, "end": v(94.46, 41.5) * mm});
            skArc(sketch, "E55.4.0.59", {"start": v(80.46, -47) * mm, "mid": v(80.76, -47.7) * mm, "end": v(81.46, -48) * mm});
            skArc(sketch, "E55.4.0.60", {"start": v(80.46, 41.5) * mm, "mid": v(80.76, 40.8) * mm, "end": v(81.46, 40.5) * mm});
            skArc(sketch, "E55.4.0.61", {"start": v(93.46, -48) * mm, "mid": v(94.17, -47.7) * mm, "end": v(94.46, -47) * mm});
            skLineSegment(sketch, "E55.direction1", {"start": v(-89.14, -48) * mm, "end": v(-46.74, -48) * mm, "construction": true});
            skSolve(sketch);
        }
        {
            var Q0;
            Q0=makeQuery(id+"F2.imprint","IMPRINT",FACE,{"disambiguationData":[TD([[makeQuery(id+"F2.imprint","IMPRINT",EDGE,{"derivedFrom":sQuery(id+"F2.wireOp",EDGE,"0Sxc741Y-Cewn-54dJ-3bVl-ir7Wj4F0T4U1.bottom")}),1.0]])]});
            var Q1;
            Q1=makeQuery(id+"F2.imprint","IMPRINT",FACE,{"disambiguationData":[TD([[makeQuery(id+"F2.imprint","IMPRINT",EDGE,{"derivedFrom":sQuery(id+"F2.wireOp",EDGE,"ad1f3a76-fd38-4dfd-9f8e-c6c0c11beda1.0.1.1")}),1.0]])]});
            var Q2;
            Q2=makeQuery(id+"F2.imprint","IMPRINT",FACE,{"disambiguationData":[TD([[makeQuery(id+"F2.imprint","IMPRINT",EDGE,{"derivedFrom":sQuery(id+"F2.wireOp",EDGE,"E16.bottom")}),1.0]])]});
            var Q3;
            Q3=makeQuery(id+"F2.imprint","IMPRINT",FACE,{"disambiguationData":[TD([[makeQuery(id+"F2.imprint","IMPRINT",EDGE,{"derivedFrom":sQuery(id+"F2.wireOp",EDGE,"ad1f3a76-fd38-4dfd-9f8e-c6c0c11beda1.1.0.1")}),1.0]])]});
            var Q4;
            Q4=makeQuery(id+"F2.imprint","IMPRINT",FACE,{"disambiguationData":[TD([[makeQuery(id+"F2.imprint","IMPRINT",EDGE,{"derivedFrom":sQuery(id+"F2.wireOp",EDGE,"ad1f3a76-fd38-4dfd-9f8e-c6c0c11beda1.1.1.1")}),1.0]])]});
            var Q5;
            Q5=makeQuery(id+"F2.imprint","IMPRINT",FACE,{"disambiguationData":[TD([[makeQuery(id+"F2.imprint","IMPRINT",EDGE,{"derivedFrom":sQuery(id+"F2.wireOp",EDGE,"32675a8e-c7b8-4809-b419-72e2611dd082.1.0.0")}),-1.0]])]});
            var Q6;
            Q6=makeQuery(id+"F2.imprint","IMPRINT",FACE,{"disambiguationData":[TD([[makeQuery(id+"F2.imprint","IMPRINT",EDGE,{"derivedFrom":sQuery(id+"F2.wireOp",EDGE,"32675a8e-c7b8-4809-b419-72e2611dd082.2.0.0")}),-1.0]])]});
            var Q7;
            Q7=makeQuery(id+"F2.imprint","IMPRINT",FACE,{"disambiguationData":[TD([[makeQuery(id+"F2.imprint","IMPRINT",EDGE,{"derivedFrom":sQuery(id+"F2.wireOp",EDGE,"ad1f3a76-fd38-4dfd-9f8e-c6c0c11beda1.2.1.1")}),1.0]])]});
            var Q8;
            Q8=makeQuery(id+"F2.imprint","IMPRINT",FACE,{"disambiguationData":[TD([[makeQuery(id+"F2.imprint","IMPRINT",EDGE,{"derivedFrom":sQuery(id+"F2.wireOp",EDGE,"ad1f3a76-fd38-4dfd-9f8e-c6c0c11beda1.2.0.1")}),1.0]])]});
            var Q9;
            Q9=makeQuery(id+"F2.imprint","IMPRINT",FACE,{"disambiguationData":[TD([[makeQuery(id+"F2.imprint","IMPRINT",EDGE,{"derivedFrom":sQuery(id+"F2.wireOp",EDGE,"ad1f3a76-fd38-4dfd-9f8e-c6c0c11beda1.3.0.1")}),1.0]])]});
            var Q10;
            Q10=makeQuery(id+"F2.imprint","IMPRINT",FACE,{"disambiguationData":[TD([[makeQuery(id+"F2.imprint","IMPRINT",EDGE,{"derivedFrom":sQuery(id+"F2.wireOp",EDGE,"ad1f3a76-fd38-4dfd-9f8e-c6c0c11beda1.3.1.1")}),1.0]])]});
            var Q11;
            Q11=makeQuery(id+"F2.imprint","IMPRINT",FACE,{"disambiguationData":[TD([[makeQuery(id+"F2.imprint","IMPRINT",EDGE,{"derivedFrom":sQuery(id+"F2.wireOp",EDGE,"32675a8e-c7b8-4809-b419-72e2611dd082.3.0.0")}),-1.0]])]});
            var Q12;
            Q12=makeQuery(id+"F2.imprint","IMPRINT",FACE,{"disambiguationData":[TD([[makeQuery(id+"F2.imprint","IMPRINT",EDGE,{"derivedFrom":sQuery(id+"F2.wireOp",EDGE,"32675a8e-c7b8-4809-b419-72e2611dd082.4.0.0")}),-1.0]])]});
            var Q13;
            Q13=makeQuery(id+"F2.imprint","IMPRINT",FACE,{"disambiguationData":[TD([[makeQuery(id+"F2.imprint","IMPRINT",EDGE,{"derivedFrom":sQuery(id+"F2.wireOp",EDGE,"ad1f3a76-fd38-4dfd-9f8e-c6c0c11beda1.4.1.1")}),1.0]])]});
            var Q14;
            Q14=makeQuery(id+"F2.imprint","IMPRINT",FACE,{"disambiguationData":[TD([[makeQuery(id+"F2.imprint","IMPRINT",EDGE,{"derivedFrom":sQuery(id+"F2.wireOp",EDGE,"ad1f3a76-fd38-4dfd-9f8e-c6c0c11beda1.4.0.1")}),1.0]])]});
            var Q15;
            Q15=makeQuery(id+"F2.imprint","IMPRINT",FACE,{"disambiguationData":[TD([[makeQuery(id+"F2.imprint","IMPRINT",EDGE,{"derivedFrom":sQuery(id+"F2.wireOp",EDGE,"32929cae-98eb-4658-b742-5b1cb45748d1.1.0.1")}),1.0]])]});
            var Q16;
            Q16=makeQuery(id+"F2.imprint","IMPRINT",FACE,{"disambiguationData":[TD([[makeQuery(id+"F2.imprint","IMPRINT",EDGE,{"derivedFrom":sQuery(id+"F2.wireOp",EDGE,"32929cae-98eb-4658-b742-5b1cb45748d1.1.0.15")}),1.0]])]});
            var Q17;
            Q17=makeQuery(id+"F2.imprint","IMPRINT",FACE,{"disambiguationData":[TD([[makeQuery(id+"F2.imprint","IMPRINT",EDGE,{"derivedFrom":sQuery(id+"F2.wireOp",EDGE,"32929cae-98eb-4658-b742-5b1cb45748d1.1.0.3")}),1.0]])]});
            var Q18;
            Q18=makeQuery(id+"F2.imprint","IMPRINT",FACE,{"disambiguationData":[TD([[makeQuery(id+"F2.imprint","IMPRINT",EDGE,{"derivedFrom":sQuery(id+"F2.wireOp",EDGE,"32929cae-98eb-4658-b742-5b1cb45748d1.2.0.3")}),1.0]])]});
            var Q19;
            Q19=makeQuery(id+"F2.imprint","IMPRINT",FACE,{"disambiguationData":[TD([[makeQuery(id+"F2.imprint","IMPRINT",EDGE,{"derivedFrom":sQuery(id+"F2.wireOp",EDGE,"32929cae-98eb-4658-b742-5b1cb45748d1.2.0.1")}),1.0]])]});
            var Q20;
            Q20=makeQuery(id+"F2.imprint","IMPRINT",FACE,{"disambiguationData":[TD([[makeQuery(id+"F2.imprint","IMPRINT",EDGE,{"derivedFrom":sQuery(id+"F2.wireOp",EDGE,"32929cae-98eb-4658-b742-5b1cb45748d1.2.0.15")}),1.0]])]});
            var Q21;
            Q21=makeQuery(id+"F2.imprint","IMPRINT",FACE,{"disambiguationData":[TD([[makeQuery(id+"F2.imprint","IMPRINT",EDGE,{"derivedFrom":sQuery(id+"F2.wireOp",EDGE,"32929cae-98eb-4658-b742-5b1cb45748d1.3.0.15")}),1.0]])]});
            var Q22;
            Q22=makeQuery(id+"F2.imprint","IMPRINT",FACE,{"disambiguationData":[TD([[makeQuery(id+"F2.imprint","IMPRINT",EDGE,{"derivedFrom":sQuery(id+"F2.wireOp",EDGE,"32929cae-98eb-4658-b742-5b1cb45748d1.3.0.1")}),1.0]])]});
            var Q23;
            Q23=makeQuery(id+"F2.imprint","IMPRINT",FACE,{"disambiguationData":[TD([[makeQuery(id+"F2.imprint","IMPRINT",EDGE,{"derivedFrom":sQuery(id+"F2.wireOp",EDGE,"32929cae-98eb-4658-b742-5b1cb45748d1.3.0.3")}),1.0]])]});
            var Q24;
            Q24=makeQuery(id+"F2.imprint","IMPRINT",FACE,{"disambiguationData":[TD([[makeQuery(id+"F2.imprint","IMPRINT",EDGE,{"derivedFrom":sQuery(id+"F2.wireOp",EDGE,"32929cae-98eb-4658-b742-5b1cb45748d1.4.0.3")}),1.0]])]});
            var Q25;
            Q25=makeQuery(id+"F2.imprint","IMPRINT",FACE,{"disambiguationData":[TD([[makeQuery(id+"F2.imprint","IMPRINT",EDGE,{"derivedFrom":sQuery(id+"F2.wireOp",EDGE,"32929cae-98eb-4658-b742-5b1cb45748d1.4.0.1")}),1.0]])]});
            var Q26;
            Q26=makeQuery(id+"F2.imprint","IMPRINT",FACE,{"disambiguationData":[TD([[makeQuery(id+"F2.imprint","IMPRINT",EDGE,{"derivedFrom":sQuery(id+"F2.wireOp",EDGE,"32929cae-98eb-4658-b742-5b1cb45748d1.4.0.15")}),1.0]])]});
            var Q27;
            Q27=makeQuery(id+"F2.imprint","IMPRINT",FACE,{"disambiguationData":[TD([[makeQuery(id+"F2.imprint","IMPRINT",EDGE,{"derivedFrom":sQuery(id+"F2.wireOp",EDGE,"E22.bottom")}),1.0]])]});
            var Q28;
            Q28=makeQuery(id+"F2.imprint","IMPRINT",FACE,{"disambiguationData":[TD([[makeQuery(id+"F2.imprint","IMPRINT",EDGE,{"derivedFrom":sQuery(id+"F2.wireOp",EDGE,"E27.bottom")}),1.0]])]});
            var Q29;
            Q29=makeQuery(id+"F2.imprint","IMPRINT",FACE,{"disambiguationData":[TD([[makeQuery(id+"F2.imprint","IMPRINT",EDGE,{"derivedFrom":sQuery(id+"F2.wireOp",EDGE,"E36.bottom")}),1.0]])]});
            var Q30;
            Q30=makeQuery(id+"F2.imprint","IMPRINT",FACE,{"disambiguationData":[TD([[makeQuery(id+"F2.imprint","IMPRINT",EDGE,{"derivedFrom":sQuery(id+"F2.wireOp",EDGE,"E41.bottom")}),1.0]])]});
            var Q31;
            Q31=makeQuery(id+"F2.imprint","IMPRINT",FACE,{"disambiguationData":[TD([[makeQuery(id+"F2.imprint","IMPRINT",EDGE,{"derivedFrom":sQuery(id+"F2.wireOp",EDGE,"E46.bottom")}),1.0]])]});
            var Q32;
            Q32=makeQuery(id+"F2.imprint","IMPRINT",FACE,{"disambiguationData":[TD([[makeQuery(id+"F2.imprint","IMPRINT",EDGE,{"derivedFrom":sQuery(id+"F2.wireOp",EDGE,"E55.1.0.7")}),-1.0]])]});
            var Q33;
            Q33=makeQuery(id+"F2.imprint","IMPRINT",FACE,{"disambiguationData":[TD([[makeQuery(id+"F2.imprint","IMPRINT",EDGE,{"derivedFrom":sQuery(id+"F2.wireOp",EDGE,"E55.1.0.2")}),-1.0]])]});
            var Q34;
            Q34=makeQuery(id+"F2.imprint","IMPRINT",FACE,{"disambiguationData":[TD([[makeQuery(id+"F2.imprint","IMPRINT",EDGE,{"derivedFrom":sQuery(id+"F2.wireOp",EDGE,"E55.1.0.9")}),1.0]])]});
            var Q35;
            Q35=makeQuery(id+"F2.imprint","IMPRINT",FACE,{"disambiguationData":[TD([[makeQuery(id+"F2.imprint","IMPRINT",EDGE,{"derivedFrom":sQuery(id+"F2.wireOp",EDGE,"E55.1.0.13")}),1.0]])]});
            var Q36;
            Q36=makeQuery(id+"F2.imprint","IMPRINT",FACE,{"disambiguationData":[TD([[makeQuery(id+"F2.imprint","IMPRINT",EDGE,{"derivedFrom":sQuery(id+"F2.wireOp",EDGE,"E55.1.0.10")}),1.0]])]});
            var Q37;
            Q37=makeQuery(id+"F2.imprint","IMPRINT",FACE,{"disambiguationData":[TD([[makeQuery(id+"F2.imprint","IMPRINT",EDGE,{"derivedFrom":sQuery(id+"F2.wireOp",EDGE,"E55.1.0.6")}),-1.0]])]});
            var Q38;
            Q38=makeQuery(id+"F2.imprint","IMPRINT",FACE,{"disambiguationData":[TD([[makeQuery(id+"F2.imprint","IMPRINT",EDGE,{"derivedFrom":sQuery(id+"F2.wireOp",EDGE,"E55.2.0.2")}),-1.0]])]});
            var Q39;
            Q39=makeQuery(id+"F2.imprint","IMPRINT",FACE,{"disambiguationData":[TD([[makeQuery(id+"F2.imprint","IMPRINT",EDGE,{"derivedFrom":sQuery(id+"F2.wireOp",EDGE,"E55.2.0.7")}),-1.0]])]});
            var Q40;
            Q40=makeQuery(id+"F2.imprint","IMPRINT",FACE,{"disambiguationData":[TD([[makeQuery(id+"F2.imprint","IMPRINT",EDGE,{"derivedFrom":sQuery(id+"F2.wireOp",EDGE,"E55.2.0.9")}),1.0]])]});
            var Q41;
            Q41=makeQuery(id+"F2.imprint","IMPRINT",FACE,{"disambiguationData":[TD([[makeQuery(id+"F2.imprint","IMPRINT",EDGE,{"derivedFrom":sQuery(id+"F2.wireOp",EDGE,"E55.2.0.10")}),1.0]])]});
            var Q42;
            Q42=makeQuery(id+"F2.imprint","IMPRINT",FACE,{"disambiguationData":[TD([[makeQuery(id+"F2.imprint","IMPRINT",EDGE,{"derivedFrom":sQuery(id+"F2.wireOp",EDGE,"E55.2.0.13")}),1.0]])]});
            var Q43;
            Q43=makeQuery(id+"F2.imprint","IMPRINT",FACE,{"disambiguationData":[TD([[makeQuery(id+"F2.imprint","IMPRINT",EDGE,{"derivedFrom":sQuery(id+"F2.wireOp",EDGE,"E55.2.0.6")}),-1.0]])]});
            var Q44;
            Q44=makeQuery(id+"F2.imprint","IMPRINT",FACE,{"disambiguationData":[TD([[makeQuery(id+"F2.imprint","IMPRINT",EDGE,{"derivedFrom":sQuery(id+"F2.wireOp",EDGE,"E55.3.0.2")}),-1.0]])]});
            var Q45;
            Q45=makeQuery(id+"F2.imprint","IMPRINT",FACE,{"disambiguationData":[TD([[makeQuery(id+"F2.imprint","IMPRINT",EDGE,{"derivedFrom":sQuery(id+"F2.wireOp",EDGE,"E55.3.0.7")}),-1.0]])]});
            var Q46;
            Q46=makeQuery(id+"F2.imprint","IMPRINT",FACE,{"disambiguationData":[TD([[makeQuery(id+"F2.imprint","IMPRINT",EDGE,{"derivedFrom":sQuery(id+"F2.wireOp",EDGE,"E55.3.0.9")}),1.0]])]});
            var Q47;
            Q47=makeQuery(id+"F2.imprint","IMPRINT",FACE,{"disambiguationData":[TD([[makeQuery(id+"F2.imprint","IMPRINT",EDGE,{"derivedFrom":sQuery(id+"F2.wireOp",EDGE,"E55.3.0.10")}),1.0]])]});
            var Q48;
            Q48=makeQuery(id+"F2.imprint","IMPRINT",FACE,{"disambiguationData":[TD([[makeQuery(id+"F2.imprint","IMPRINT",EDGE,{"derivedFrom":sQuery(id+"F2.wireOp",EDGE,"E55.3.0.6")}),-1.0]])]});
            var Q49;
            Q49=makeQuery(id+"F2.imprint","IMPRINT",FACE,{"disambiguationData":[TD([[makeQuery(id+"F2.imprint","IMPRINT",EDGE,{"derivedFrom":sQuery(id+"F2.wireOp",EDGE,"E55.4.0.2")}),-1.0]])]});
            var Q50;
            Q50=makeQuery(id+"F2.imprint","IMPRINT",FACE,{"disambiguationData":[TD([[makeQuery(id+"F2.imprint","IMPRINT",EDGE,{"derivedFrom":sQuery(id+"F2.wireOp",EDGE,"E55.4.0.7")}),-1.0]])]});
            var Q51;
            Q51=makeQuery(id+"F2.imprint","IMPRINT",FACE,{"disambiguationData":[TD([[makeQuery(id+"F2.imprint","IMPRINT",EDGE,{"derivedFrom":sQuery(id+"F2.wireOp",EDGE,"E55.4.0.9")}),1.0]])]});
            var Q52;
            Q52=makeQuery(id+"F2.imprint","IMPRINT",FACE,{"disambiguationData":[TD([[makeQuery(id+"F2.imprint","IMPRINT",EDGE,{"derivedFrom":sQuery(id+"F2.wireOp",EDGE,"E55.3.0.13")}),1.0]])]});
            extrude(context, id + "F3", {"entities" : qUnion([Q0, Q1, Q2, Q3, Q4, Q5, Q6, Q7, Q8, Q9, Q10, Q11, Q12, Q13, Q14, Q15, Q16, Q17, Q18, Q19, Q20, Q21, Q22, Q23, Q24, Q25, Q26, Q27, Q28, Q29, Q30, Q31, Q32, Q33, Q34, Q35, Q36, Q37, Q38, Q39, Q40, Q41, Q42, Q43, Q44, Q45, Q46, Q47, Q48, Q49, Q50, Q51, Q52]), "operationType" : NewBodyOperationType.REMOVE, "endBound" : BoundingType.THROUGH_ALL, "oppositeDirection" : true, "depth" : 25 * mm, "offsetDistance" : 25 * mm});
        }
    });
